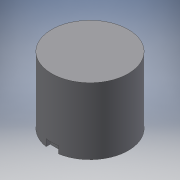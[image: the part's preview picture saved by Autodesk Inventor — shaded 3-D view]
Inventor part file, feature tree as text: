
AUTODESK INVENTOR PART (.ipt)
format: ipt  version: 2016 (Build 200138000, 138)  size: 129,024 bytes
history: native  units: mm
features: extrude x4, sketch x4
ambient origin geometry x8: Origin, YZ Plane, XZ Plane, XY Plane, X Axis, Y Axis, Z Axis, Center Point
bodies: Solide1 (feature_tree)
feature tree (8):
  extrude  "Extrusion1"  Depth=27.0mm
  extrude  "Extrusion2"  Depth=16.5mm
  extrude  "Extrusion3"  Depth=23.5mm TaperAngle=0.0deg
  extrude  "Extrusion4"  Depth=1.3mm TaperAngle=0.0deg
  sketch  "Esquisse1"
  sketch  "Esquisse2"
  sketch  "Esquisse3"
  sketch  "Esquisse4"
